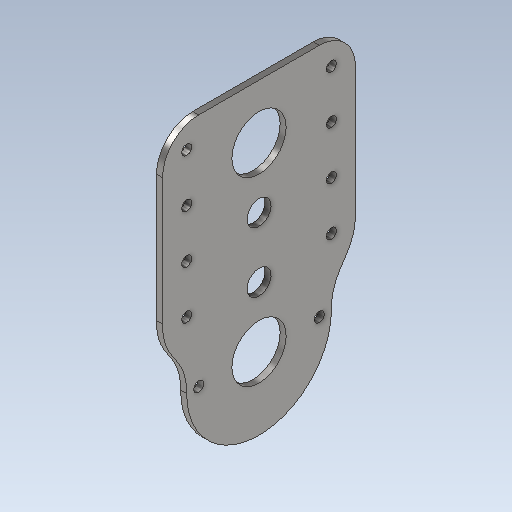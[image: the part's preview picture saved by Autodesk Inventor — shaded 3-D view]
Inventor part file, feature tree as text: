
AUTODESK INVENTOR PART (.ipt)
format: ipt  version: 2023 (Build 270158000, 158)  size: 159,232 bytes
history: native  units: in
note: dims shown in document units (in); Inventor stores cm internally (conversion verified against a paired STEP export)
features: other x3, sketch x1
ambient origin geometry x8: Origin, YZ Plane, XZ Plane, XY Plane, X Axis, Y Axis, Z Axis, Center Point
bodies: Solid1 (feature_tree)
feature tree (4):
  other  "L1Plate.ipt"
  other  "Solid1::L1Plate.ipt"
  other  "TaggingFeature1"
  sketch  "Sketch1"  dims[d0=0.3937in]
